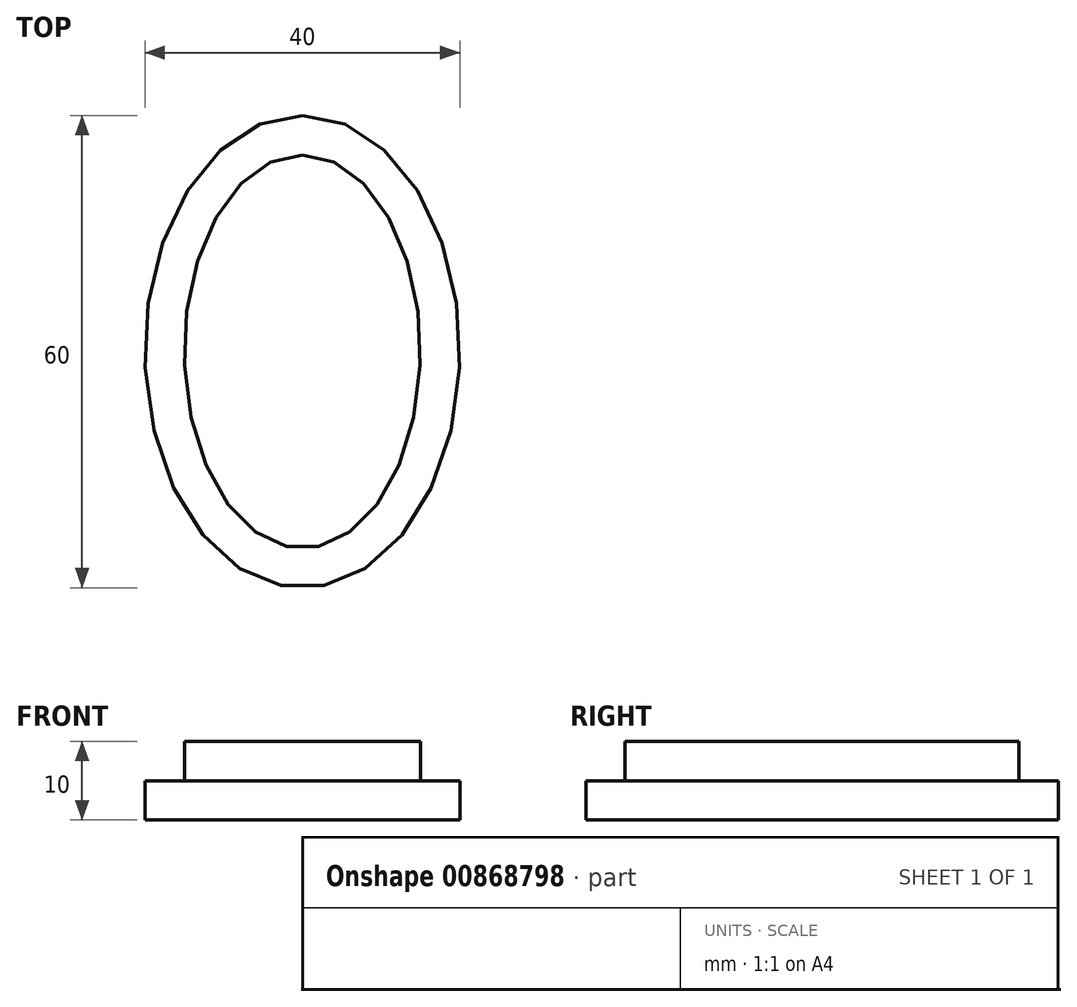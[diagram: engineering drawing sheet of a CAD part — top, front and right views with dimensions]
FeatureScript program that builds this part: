
annotation { "Feature Type Name" : "Feature", "Feature Type Description" : "" }
export const myFeature = defineFeature(function(context is Context, id is Id, definition is map)
    precondition{}
    {
        {
            var Q0;
            Q0=qCreatedBy(makeId("Top.planeOp"),FACE);
            var sketch = newSketch(context, id + "F0", { "sketchPlane" : qUnion([Q0])});
            skEllipse(sketch, "E0", {"center": v(0, 0) * mm, "majorRadius": 30 * mm, "minorRadius": 20 * mm, "majorAxis": v(0, 1)});
            skSolve(sketch);
        }
        {
            var Q0;
            Q0=makeQuery(id+"F0.imprint","IMPRINT",FACE,{"disambiguationData":[TD([[makeQuery(id+"F0.imprint","IMPRINT",EDGE,{"derivedFrom":sQuery(id+"F0.wireOp",EDGE,"E0")}),1.0]])]});
            extrude(context, id + "F1", {"entities" : qUnion([Q0]), "depth" : 5 * mm, "offsetDistance" : 25 * mm});
        }
        {
            var Q0;
            Q0=makeQuery(id+"F1.opExtrude","CAP_FACE",FACE,{"disambiguationData":[OSD([sQuery(id+"F0.wireOp",EDGE,"E0")])],"isStart":false});
            var sketch = newSketch(context, id + "F2", { "sketchPlane" : qUnion([Q0])});
            skEllipse(sketch, "E1", {"center": v(0, 0) * mm, "majorRadius": 25 * mm, "minorRadius": 15 * mm, "majorAxis": v(0, 1)});
            skSolve(sketch);
        }
        {
            var Q0;
            Q0=makeQuery(id+"F2.imprint","IMPRINT",FACE,{"disambiguationData":[TD([[makeQuery(id+"F2.imprint","IMPRINT",EDGE,{"derivedFrom":sQuery(id+"F2.wireOp",EDGE,"E1")}),1.0]])]});
            extrude(context, id + "F3", {"entities" : qUnion([Q0]), "operationType" : NewBodyOperationType.ADD, "depth" : 5 * mm, "offsetDistance" : 25 * mm});
        }
    });
